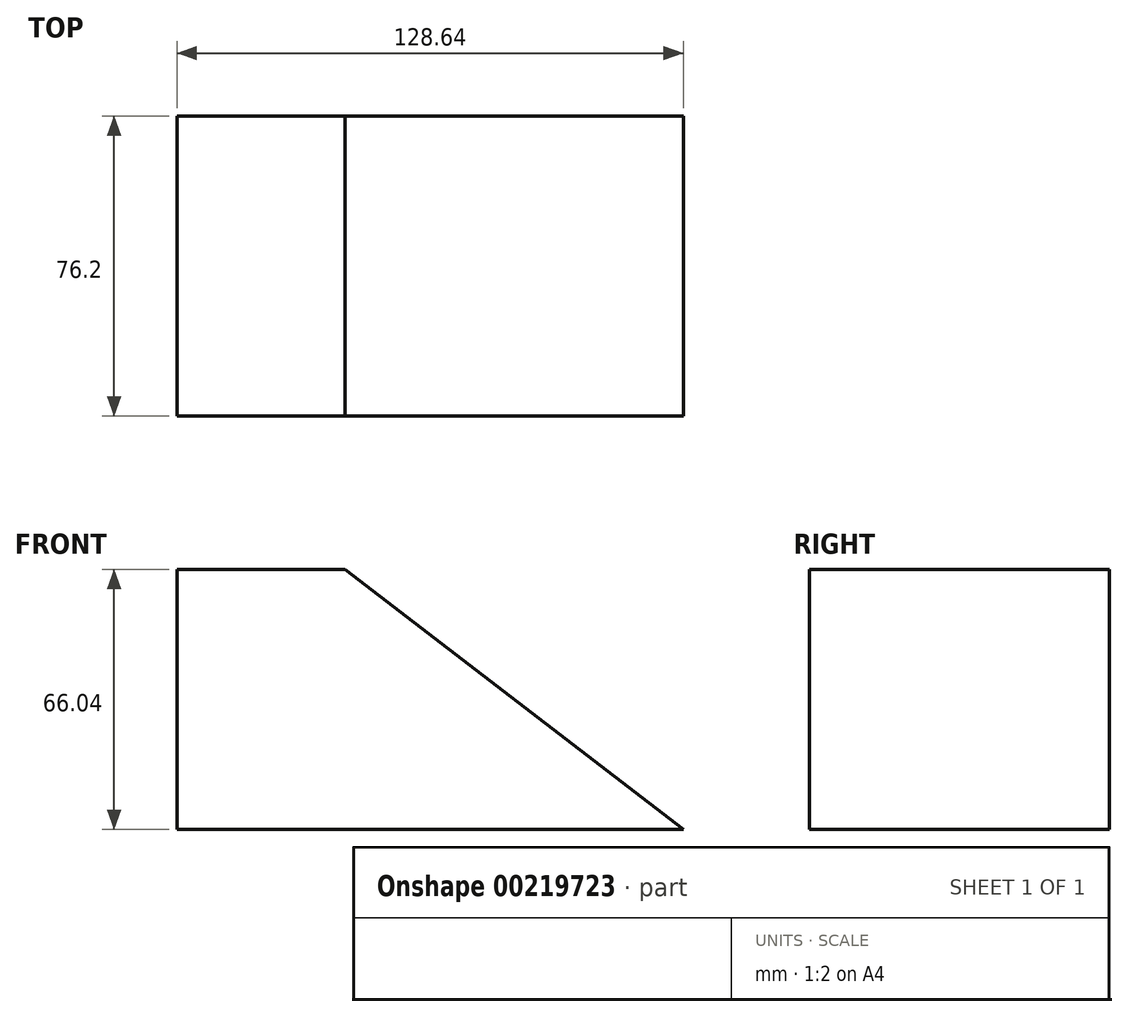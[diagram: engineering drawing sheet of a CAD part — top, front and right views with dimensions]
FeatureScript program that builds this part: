
annotation { "Feature Type Name" : "Feature", "Feature Type Description" : "" }
export const myFeature = defineFeature(function(context is Context, id is Id, definition is map)
    precondition{}
    {
        {
            var Q0;
            Q0=qCreatedBy(makeId("Front.planeOp"),FACE);
            var sketch = newSketch(context, id + "F0", { "sketchPlane" : qUnion([Q0])});
            skLineSegment(sketch, "E0.bottom", {"start": v(64.32, 33.02) * mm, "end": v(-64.32, 33.02) * mm});
            skLineSegment(sketch, "E0.top", {"start": v(64.32, -33.02) * mm, "end": v(-64.32, -33.02) * mm});
            skLineSegment(sketch, "E0.left", {"start": v(64.32, 33.02) * mm, "end": v(64.32, -33.02) * mm});
            skLineSegment(sketch, "E0.right", {"start": v(-64.32, 33.02) * mm, "end": v(-64.32, -33.02) * mm});
            skPoint(sketch, "E0.middle", {"position": v(0, 0) * mm});
            skSolve(sketch);
        }
        {
            var Q0;
            Q0=makeQuery(id+"F0.imprint","IMPRINT",FACE,{"disambiguationData":[TD([[makeQuery(id+"F0.imprint","IMPRINT",EDGE,{"derivedFrom":sQuery(id+"F0.wireOp",EDGE,"E0.bottom")}),1.0]])]});
            extrude(context, id + "F1", {"entities" : qUnion([Q0]), "depth" : 76.2 * mm});
        }
        {
            var Q0;
            Q0=makeQuery(id+"F1.opExtrude","CAP_FACE",FACE,{"disambiguationData":[OSD([sQuery(id+"F0.wireOp",EDGE,"E0.bottom"),sQuery(id+"F0.wireOp",EDGE,"E0.top"),sQuery(id+"F0.wireOp",EDGE,"E0.left"),sQuery(id+"F0.wireOp",EDGE,"E0.right")])],"isStart":false});
            var sketch = newSketch(context, id + "F2", { "sketchPlane" : qUnion([Q0])});
            skLineSegment(sketch, "E1.0", {"start": v(64.32, 33.02) * mm, "end": v(-64.32, 33.02) * mm});
            skLineSegment(sketch, "E2.0", {"start": v(64.32, 33.02) * mm, "end": v(64.32, -33.02) * mm});
            skLineSegment(sketch, "E3", {"start": v(-21.57, 33.02) * mm, "end": v(64.32, -33.02) * mm});
            skSolve(sketch);
        }
        {
            var Q0;
            {var subQ0=sQuery(id+"F2.wireOp",EDGE,"E2.0");Q0=makeQuery(id+"F2.imprint","IMPRINT",FACE,{"disambiguationData":[TD([[makeQuery(id+"F2.imprint","IMPRINT",EDGE,{"derivedFrom":subQ0}),-1.0]])]});}
            extrude(context, id + "F3", {"entities" : qUnion([Q0]), "operationType" : NewBodyOperationType.REMOVE, "endBound" : BoundingType.THROUGH_ALL, "oppositeDirection" : true, "depth" : 76.2 * mm});
        }
    });
